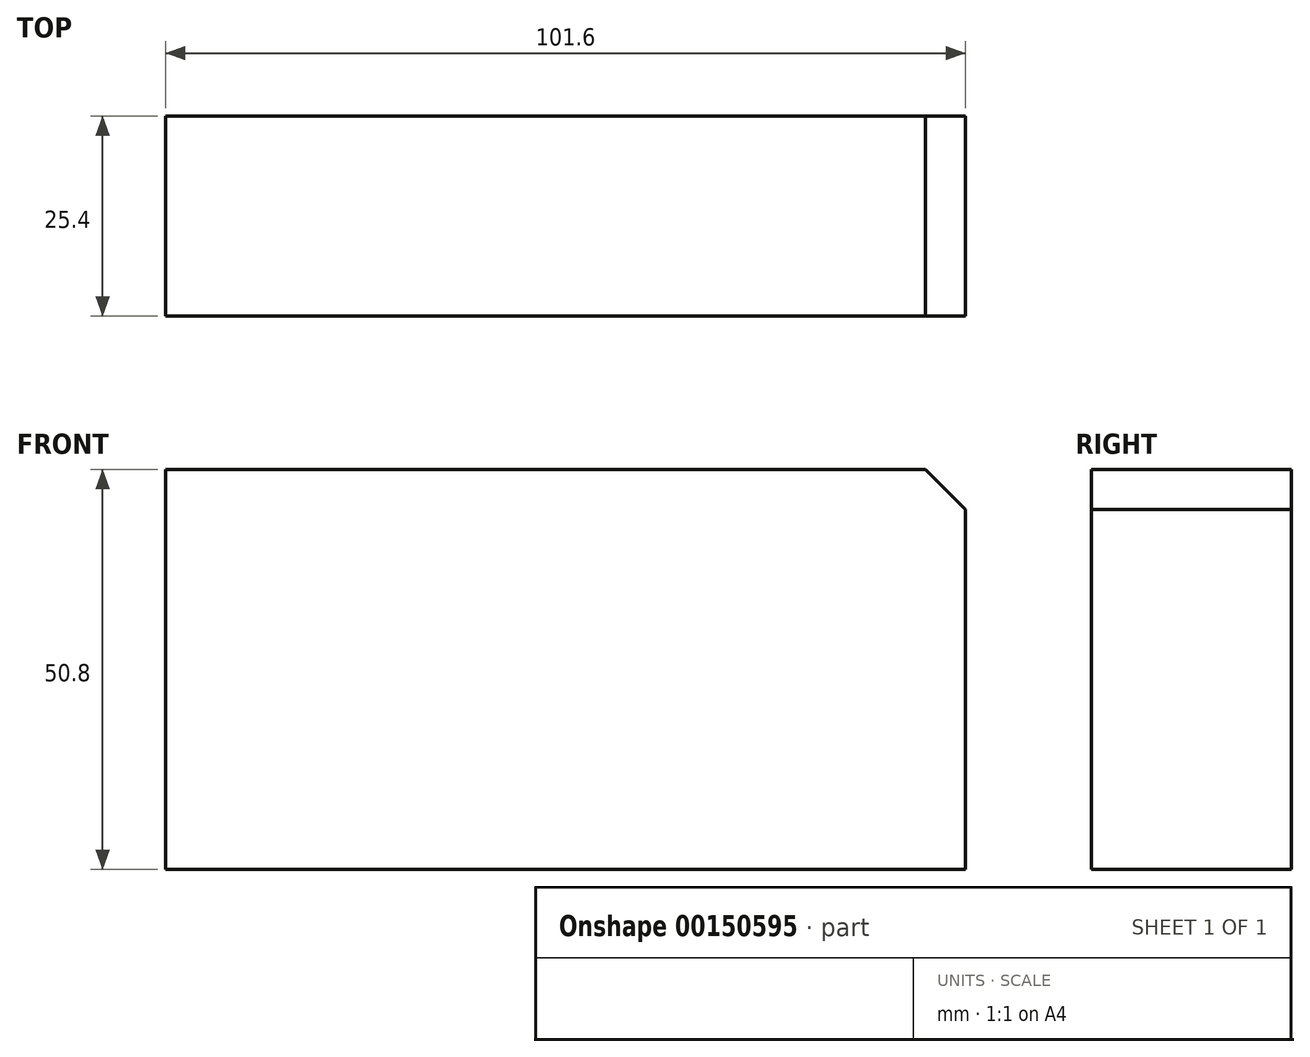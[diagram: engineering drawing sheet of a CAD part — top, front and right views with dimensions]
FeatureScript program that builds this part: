
annotation { "Feature Type Name" : "Feature", "Feature Type Description" : "" }
export const myFeature = defineFeature(function(context is Context, id is Id, definition is map)
    precondition{}
    {
        {
            var Q0;
            Q0=qCreatedBy(makeId("Front.planeOp"),FACE);
            var sketch = newSketch(context, id + "F0", { "sketchPlane" : qUnion([Q0])});
            skLineSegment(sketch, "E0.bottom", {"start": v(-41.46, 24.46) * mm, "end": v(60.14, 24.46) * mm});
            skLineSegment(sketch, "E0.top", {"start": v(-41.46, -26.34) * mm, "end": v(60.14, -26.34) * mm});
            skLineSegment(sketch, "E0.left", {"start": v(-41.46, 24.46) * mm, "end": v(-41.46, -26.34) * mm});
            skLineSegment(sketch, "E0.right", {"start": v(60.14, 24.46) * mm, "end": v(60.14, -26.34) * mm});
            skSolve(sketch);
        }
        {
            var Q0;
            Q0 = qSketchRegion(id + "F0", true);
            extrude(context, id + "F1", {"entities" : qUnion([Q0]), "depth" : 25.4 * mm});
        }
        {
            var Q0;
            Q0=makeQuery(id+"F1.opExtrude","SWEPT_EDGE",EDGE,{"disambiguationData":[OSD([sQuery(id+"F0.wireOp",EDGE,"E0.bottom"),sQuery(id+"F0.wireOp",EDGE,"E0.right")])]});
            chamfer(context, id + "F2", {"entities" : qUnion([Q0]), "width" : 5.08 * mm, "tangentPropagation" : true});
        }
    });
